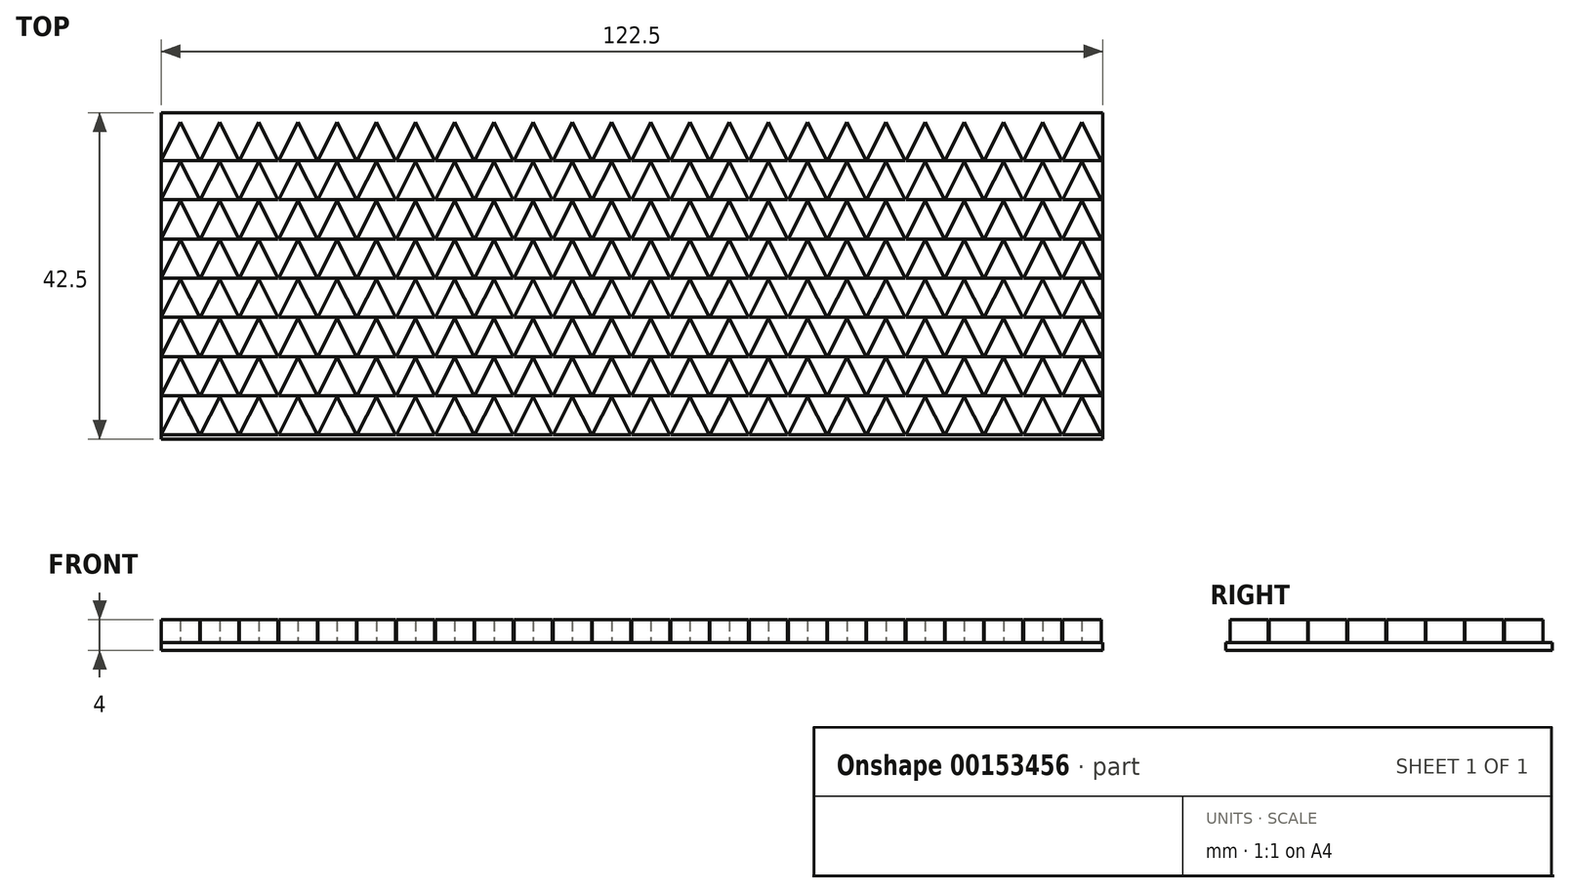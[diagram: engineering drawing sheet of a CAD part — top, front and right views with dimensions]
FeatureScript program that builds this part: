
annotation { "Feature Type Name" : "Feature", "Feature Type Description" : "" }
export const myFeature = defineFeature(function(context is Context, id is Id, definition is map)
    precondition{}
    {
        {
            var Q0;
            Q0=qCreatedBy(makeId("Top.planeOp"),FACE);
            var sketch = newSketch(context, id + "F0", { "sketchPlane" : qUnion([Q0])});
            skLineSegment(sketch, "E0.bottom", {"start": v(61.25, -21.25) * mm, "end": v(-61.25, -21.25) * mm});
            skLineSegment(sketch, "E0.top", {"start": v(61.25, 21.25) * mm, "end": v(-61.25, 21.25) * mm});
            skLineSegment(sketch, "E0.left", {"start": v(61.25, -21.25) * mm, "end": v(61.25, 21.25) * mm});
            skLineSegment(sketch, "E0.right", {"start": v(-61.25, -21.25) * mm, "end": v(-61.25, 21.25) * mm});
            skPoint(sketch, "E0.middle", {"position": v(0, 0) * mm});
            skSolve(sketch);
        }
        {
            var Q0;
            Q0=makeQuery(id+"F0.imprint","IMPRINT",FACE,{"disambiguationData":[TD([[makeQuery(id+"F0.imprint","IMPRINT",EDGE,{"derivedFrom":sQuery(id+"F0.wireOp",EDGE,"E0.bottom")}),-1.0]])]});
            extrude(context, id + "F1", {"entities" : qUnion([Q0]), "depth" : 1 * mm});
        }
        {
            var Q0;
            Q0=makeQuery(id+"F1.opExtrude","CAP_FACE",FACE,{"disambiguationData":[OSD([sQuery(id+"F0.wireOp",EDGE,"E0.bottom"),sQuery(id+"F0.wireOp",EDGE,"E0.top"),sQuery(id+"F0.wireOp",EDGE,"E0.left"),sQuery(id+"F0.wireOp",EDGE,"E0.right")])],"isStart":false});
            var sketch = newSketch(context, id + "F2", { "sketchPlane" : qUnion([Q0])});
            skLineSegment(sketch, "E1.top", {"start": v(-61.25, 15) * mm, "end": v(-56.25, 15) * mm});
            skLineSegment(sketch, "E2", {"start": v(-61.25, 15) * mm, "end": v(-58.75, 20) * mm});
            skLineSegment(sketch, "E3", {"start": v(-58.75, 20) * mm, "end": v(-56.25, 15) * mm});
            skLineSegment(sketch, "E4.0.1.0", {"start": v(-58.75, 14.9) * mm, "end": v(-56.25, 9.9) * mm});
            skLineSegment(sketch, "E4.0.1.1", {"start": v(-61.25, 9.9) * mm, "end": v(-56.25, 9.9) * mm});
            skLineSegment(sketch, "E4.0.1.2", {"start": v(-61.25, 9.9) * mm, "end": v(-58.75, 14.9) * mm});
            skLineSegment(sketch, "E4.0.2.0", {"start": v(-58.75, 9.8) * mm, "end": v(-56.25, 4.8) * mm});
            skLineSegment(sketch, "E4.0.2.1", {"start": v(-61.25, 4.8) * mm, "end": v(-56.25, 4.8) * mm});
            skLineSegment(sketch, "E4.0.2.2", {"start": v(-61.25, 4.8) * mm, "end": v(-58.75, 9.8) * mm});
            skLineSegment(sketch, "E4.0.3.0", {"start": v(-58.75, 4.7) * mm, "end": v(-56.25, -0.3) * mm});
            skLineSegment(sketch, "E4.0.3.1", {"start": v(-61.25, -0.3) * mm, "end": v(-56.25, -0.3) * mm});
            skLineSegment(sketch, "E4.0.3.2", {"start": v(-61.25, -0.3) * mm, "end": v(-58.75, 4.7) * mm});
            skLineSegment(sketch, "E4.0.4.0", {"start": v(-58.75, -0.4) * mm, "end": v(-56.25, -5.4) * mm});
            skLineSegment(sketch, "E4.0.4.1", {"start": v(-61.25, -5.4) * mm, "end": v(-56.25, -5.4) * mm});
            skLineSegment(sketch, "E4.0.4.2", {"start": v(-61.25, -5.4) * mm, "end": v(-58.75, -0.4) * mm});
            skLineSegment(sketch, "E4.0.5.0", {"start": v(-58.75, -5.5) * mm, "end": v(-56.25, -10.5) * mm});
            skLineSegment(sketch, "E4.0.5.1", {"start": v(-61.25, -10.5) * mm, "end": v(-56.25, -10.5) * mm});
            skLineSegment(sketch, "E4.0.5.2", {"start": v(-61.25, -10.5) * mm, "end": v(-58.75, -5.5) * mm});
            skLineSegment(sketch, "E4.0.6.0", {"start": v(-58.75, -10.6) * mm, "end": v(-56.25, -15.6) * mm});
            skLineSegment(sketch, "E4.0.6.1", {"start": v(-61.25, -15.6) * mm, "end": v(-56.25, -15.6) * mm});
            skLineSegment(sketch, "E4.0.6.2", {"start": v(-61.25, -15.6) * mm, "end": v(-58.75, -10.6) * mm});
            skLineSegment(sketch, "E4.0.7.0", {"start": v(-58.75, -15.7) * mm, "end": v(-56.25, -20.7) * mm});
            skLineSegment(sketch, "E4.0.7.1", {"start": v(-61.25, -20.7) * mm, "end": v(-56.25, -20.7) * mm});
            skLineSegment(sketch, "E4.0.7.2", {"start": v(-61.25, -20.7) * mm, "end": v(-58.75, -15.7) * mm});
            skLineSegment(sketch, "E4.1.0.0", {"start": v(-53.65, 20) * mm, "end": v(-51.15, 15) * mm});
            skLineSegment(sketch, "E4.1.0.1", {"start": v(-56.15, 15) * mm, "end": v(-51.15, 15) * mm});
            skLineSegment(sketch, "E4.1.0.2", {"start": v(-56.15, 15) * mm, "end": v(-53.65, 20) * mm});
            skLineSegment(sketch, "E4.1.1.0", {"start": v(-53.65, 14.9) * mm, "end": v(-51.15, 9.9) * mm});
            skLineSegment(sketch, "E4.1.1.1", {"start": v(-56.15, 9.9) * mm, "end": v(-51.15, 9.9) * mm});
            skLineSegment(sketch, "E4.1.1.2", {"start": v(-56.15, 9.9) * mm, "end": v(-53.65, 14.9) * mm});
            skLineSegment(sketch, "E4.1.2.0", {"start": v(-53.65, 9.8) * mm, "end": v(-51.15, 4.8) * mm});
            skLineSegment(sketch, "E4.1.2.1", {"start": v(-56.15, 4.8) * mm, "end": v(-51.15, 4.8) * mm});
            skLineSegment(sketch, "E4.1.2.2", {"start": v(-56.15, 4.8) * mm, "end": v(-53.65, 9.8) * mm});
            skLineSegment(sketch, "E4.1.3.0", {"start": v(-53.65, 4.7) * mm, "end": v(-51.15, -0.3) * mm});
            skLineSegment(sketch, "E4.1.3.1", {"start": v(-56.15, -0.3) * mm, "end": v(-51.15, -0.3) * mm});
            skLineSegment(sketch, "E4.1.3.2", {"start": v(-56.15, -0.3) * mm, "end": v(-53.65, 4.7) * mm});
            skLineSegment(sketch, "E4.1.4.0", {"start": v(-53.65, -0.4) * mm, "end": v(-51.15, -5.4) * mm});
            skLineSegment(sketch, "E4.1.4.1", {"start": v(-56.15, -5.4) * mm, "end": v(-51.15, -5.4) * mm});
            skLineSegment(sketch, "E4.1.4.2", {"start": v(-56.15, -5.4) * mm, "end": v(-53.65, -0.4) * mm});
            skLineSegment(sketch, "E4.1.5.0", {"start": v(-53.65, -5.5) * mm, "end": v(-51.15, -10.5) * mm});
            skLineSegment(sketch, "E4.1.5.1", {"start": v(-56.15, -10.5) * mm, "end": v(-51.15, -10.5) * mm});
            skLineSegment(sketch, "E4.1.5.2", {"start": v(-56.15, -10.5) * mm, "end": v(-53.65, -5.5) * mm});
            skLineSegment(sketch, "E4.1.6.0", {"start": v(-53.65, -10.6) * mm, "end": v(-51.15, -15.6) * mm});
            skLineSegment(sketch, "E4.1.6.1", {"start": v(-56.15, -15.6) * mm, "end": v(-51.15, -15.6) * mm});
            skLineSegment(sketch, "E4.1.6.2", {"start": v(-56.15, -15.6) * mm, "end": v(-53.65, -10.6) * mm});
            skLineSegment(sketch, "E4.1.7.0", {"start": v(-53.65, -15.7) * mm, "end": v(-51.15, -20.7) * mm});
            skLineSegment(sketch, "E4.1.7.1", {"start": v(-56.15, -20.7) * mm, "end": v(-51.15, -20.7) * mm});
            skLineSegment(sketch, "E4.1.7.2", {"start": v(-56.15, -20.7) * mm, "end": v(-53.65, -15.7) * mm});
            skLineSegment(sketch, "E4.2.0.0", {"start": v(-48.55, 20) * mm, "end": v(-46.05, 15) * mm});
            skLineSegment(sketch, "E4.2.0.1", {"start": v(-51.05, 15) * mm, "end": v(-46.05, 15) * mm});
            skLineSegment(sketch, "E4.2.0.2", {"start": v(-51.05, 15) * mm, "end": v(-48.55, 20) * mm});
            skLineSegment(sketch, "E4.2.1.0", {"start": v(-48.55, 14.9) * mm, "end": v(-46.05, 9.9) * mm});
            skLineSegment(sketch, "E4.2.1.1", {"start": v(-51.05, 9.9) * mm, "end": v(-46.05, 9.9) * mm});
            skLineSegment(sketch, "E4.2.1.2", {"start": v(-51.05, 9.9) * mm, "end": v(-48.55, 14.9) * mm});
            skLineSegment(sketch, "E4.2.2.0", {"start": v(-48.55, 9.8) * mm, "end": v(-46.05, 4.8) * mm});
            skLineSegment(sketch, "E4.2.2.1", {"start": v(-51.05, 4.8) * mm, "end": v(-46.05, 4.8) * mm});
            skLineSegment(sketch, "E4.2.2.2", {"start": v(-51.05, 4.8) * mm, "end": v(-48.55, 9.8) * mm});
            skLineSegment(sketch, "E4.2.3.0", {"start": v(-48.55, 4.7) * mm, "end": v(-46.05, -0.3) * mm});
            skLineSegment(sketch, "E4.2.3.1", {"start": v(-51.05, -0.3) * mm, "end": v(-46.05, -0.3) * mm});
            skLineSegment(sketch, "E4.2.3.2", {"start": v(-51.05, -0.3) * mm, "end": v(-48.55, 4.7) * mm});
            skLineSegment(sketch, "E4.2.4.0", {"start": v(-48.55, -0.4) * mm, "end": v(-46.05, -5.4) * mm});
            skLineSegment(sketch, "E4.2.4.1", {"start": v(-51.05, -5.4) * mm, "end": v(-46.05, -5.4) * mm});
            skLineSegment(sketch, "E4.2.4.2", {"start": v(-51.05, -5.4) * mm, "end": v(-48.55, -0.4) * mm});
            skLineSegment(sketch, "E4.2.5.0", {"start": v(-48.55, -5.5) * mm, "end": v(-46.05, -10.5) * mm});
            skLineSegment(sketch, "E4.2.5.1", {"start": v(-51.05, -10.5) * mm, "end": v(-46.05, -10.5) * mm});
            skLineSegment(sketch, "E4.2.5.2", {"start": v(-51.05, -10.5) * mm, "end": v(-48.55, -5.5) * mm});
            skLineSegment(sketch, "E4.2.6.0", {"start": v(-48.55, -10.6) * mm, "end": v(-46.05, -15.6) * mm});
            skLineSegment(sketch, "E4.2.6.1", {"start": v(-51.05, -15.6) * mm, "end": v(-46.05, -15.6) * mm});
            skLineSegment(sketch, "E4.2.6.2", {"start": v(-51.05, -15.6) * mm, "end": v(-48.55, -10.6) * mm});
            skLineSegment(sketch, "E4.2.7.0", {"start": v(-48.55, -15.7) * mm, "end": v(-46.05, -20.7) * mm});
            skLineSegment(sketch, "E4.2.7.1", {"start": v(-51.05, -20.7) * mm, "end": v(-46.05, -20.7) * mm});
            skLineSegment(sketch, "E4.2.7.2", {"start": v(-51.05, -20.7) * mm, "end": v(-48.55, -15.7) * mm});
            skLineSegment(sketch, "E4.3.0.0", {"start": v(-43.45, 20) * mm, "end": v(-40.95, 15) * mm});
            skLineSegment(sketch, "E4.3.0.1", {"start": v(-45.95, 15) * mm, "end": v(-40.95, 15) * mm});
            skLineSegment(sketch, "E4.3.0.2", {"start": v(-45.95, 15) * mm, "end": v(-43.45, 20) * mm});
            skLineSegment(sketch, "E4.3.1.0", {"start": v(-43.45, 14.9) * mm, "end": v(-40.95, 9.9) * mm});
            skLineSegment(sketch, "E4.3.1.1", {"start": v(-45.95, 9.9) * mm, "end": v(-40.95, 9.9) * mm});
            skLineSegment(sketch, "E4.3.1.2", {"start": v(-45.95, 9.9) * mm, "end": v(-43.45, 14.9) * mm});
            skLineSegment(sketch, "E4.3.2.0", {"start": v(-43.45, 9.8) * mm, "end": v(-40.95, 4.8) * mm});
            skLineSegment(sketch, "E4.3.2.1", {"start": v(-45.95, 4.8) * mm, "end": v(-40.95, 4.8) * mm});
            skLineSegment(sketch, "E4.3.2.2", {"start": v(-45.95, 4.8) * mm, "end": v(-43.45, 9.8) * mm});
            skLineSegment(sketch, "E4.3.3.0", {"start": v(-43.45, 4.7) * mm, "end": v(-40.95, -0.3) * mm});
            skLineSegment(sketch, "E4.3.3.1", {"start": v(-45.95, -0.3) * mm, "end": v(-40.95, -0.3) * mm});
            skLineSegment(sketch, "E4.3.3.2", {"start": v(-45.95, -0.3) * mm, "end": v(-43.45, 4.7) * mm});
            skLineSegment(sketch, "E4.3.4.0", {"start": v(-43.45, -0.4) * mm, "end": v(-40.95, -5.4) * mm});
            skLineSegment(sketch, "E4.3.4.1", {"start": v(-45.95, -5.4) * mm, "end": v(-40.95, -5.4) * mm});
            skLineSegment(sketch, "E4.3.4.2", {"start": v(-45.95, -5.4) * mm, "end": v(-43.45, -0.4) * mm});
            skLineSegment(sketch, "E4.3.5.0", {"start": v(-43.45, -5.5) * mm, "end": v(-40.95, -10.5) * mm});
            skLineSegment(sketch, "E4.3.5.1", {"start": v(-45.95, -10.5) * mm, "end": v(-40.95, -10.5) * mm});
            skLineSegment(sketch, "E4.3.5.2", {"start": v(-45.95, -10.5) * mm, "end": v(-43.45, -5.5) * mm});
            skLineSegment(sketch, "E4.3.6.0", {"start": v(-43.45, -10.6) * mm, "end": v(-40.95, -15.6) * mm});
            skLineSegment(sketch, "E4.3.6.1", {"start": v(-45.95, -15.6) * mm, "end": v(-40.95, -15.6) * mm});
            skLineSegment(sketch, "E4.3.6.2", {"start": v(-45.95, -15.6) * mm, "end": v(-43.45, -10.6) * mm});
            skLineSegment(sketch, "E4.3.7.0", {"start": v(-43.45, -15.7) * mm, "end": v(-40.95, -20.7) * mm});
            skLineSegment(sketch, "E4.3.7.1", {"start": v(-45.95, -20.7) * mm, "end": v(-40.95, -20.7) * mm});
            skLineSegment(sketch, "E4.3.7.2", {"start": v(-45.95, -20.7) * mm, "end": v(-43.45, -15.7) * mm});
            skLineSegment(sketch, "E4.4.0.0", {"start": v(-38.35, 20) * mm, "end": v(-35.85, 15) * mm});
            skLineSegment(sketch, "E4.4.0.1", {"start": v(-40.85, 15) * mm, "end": v(-35.85, 15) * mm});
            skLineSegment(sketch, "E4.4.0.2", {"start": v(-40.85, 15) * mm, "end": v(-38.35, 20) * mm});
            skLineSegment(sketch, "E4.4.1.0", {"start": v(-38.35, 14.9) * mm, "end": v(-35.85, 9.9) * mm});
            skLineSegment(sketch, "E4.4.1.1", {"start": v(-40.85, 9.9) * mm, "end": v(-35.85, 9.9) * mm});
            skLineSegment(sketch, "E4.4.1.2", {"start": v(-40.85, 9.9) * mm, "end": v(-38.35, 14.9) * mm});
            skLineSegment(sketch, "E4.4.2.0", {"start": v(-38.35, 9.8) * mm, "end": v(-35.85, 4.8) * mm});
            skLineSegment(sketch, "E4.4.2.1", {"start": v(-40.85, 4.8) * mm, "end": v(-35.85, 4.8) * mm});
            skLineSegment(sketch, "E4.4.2.2", {"start": v(-40.85, 4.8) * mm, "end": v(-38.35, 9.8) * mm});
            skLineSegment(sketch, "E4.4.3.0", {"start": v(-38.35, 4.7) * mm, "end": v(-35.85, -0.3) * mm});
            skLineSegment(sketch, "E4.4.3.1", {"start": v(-40.85, -0.3) * mm, "end": v(-35.85, -0.3) * mm});
            skLineSegment(sketch, "E4.4.3.2", {"start": v(-40.85, -0.3) * mm, "end": v(-38.35, 4.7) * mm});
            skLineSegment(sketch, "E4.4.4.0", {"start": v(-38.35, -0.4) * mm, "end": v(-35.85, -5.4) * mm});
            skLineSegment(sketch, "E4.4.4.1", {"start": v(-40.85, -5.4) * mm, "end": v(-35.85, -5.4) * mm});
            skLineSegment(sketch, "E4.4.4.2", {"start": v(-40.85, -5.4) * mm, "end": v(-38.35, -0.4) * mm});
            skLineSegment(sketch, "E4.4.5.0", {"start": v(-38.35, -5.5) * mm, "end": v(-35.85, -10.5) * mm});
            skLineSegment(sketch, "E4.4.5.1", {"start": v(-40.85, -10.5) * mm, "end": v(-35.85, -10.5) * mm});
            skLineSegment(sketch, "E4.4.5.2", {"start": v(-40.85, -10.5) * mm, "end": v(-38.35, -5.5) * mm});
            skLineSegment(sketch, "E4.4.6.0", {"start": v(-38.35, -10.6) * mm, "end": v(-35.85, -15.6) * mm});
            skLineSegment(sketch, "E4.4.6.1", {"start": v(-40.85, -15.6) * mm, "end": v(-35.85, -15.6) * mm});
            skLineSegment(sketch, "E4.4.6.2", {"start": v(-40.85, -15.6) * mm, "end": v(-38.35, -10.6) * mm});
            skLineSegment(sketch, "E4.4.7.0", {"start": v(-38.35, -15.7) * mm, "end": v(-35.85, -20.7) * mm});
            skLineSegment(sketch, "E4.4.7.1", {"start": v(-40.85, -20.7) * mm, "end": v(-35.85, -20.7) * mm});
            skLineSegment(sketch, "E4.4.7.2", {"start": v(-40.85, -20.7) * mm, "end": v(-38.35, -15.7) * mm});
            skLineSegment(sketch, "E4.5.0.0", {"start": v(-33.25, 20) * mm, "end": v(-30.75, 15) * mm});
            skLineSegment(sketch, "E4.5.0.1", {"start": v(-35.75, 15) * mm, "end": v(-30.75, 15) * mm});
            skLineSegment(sketch, "E4.5.0.2", {"start": v(-35.75, 15) * mm, "end": v(-33.25, 20) * mm});
            skLineSegment(sketch, "E4.5.1.0", {"start": v(-33.25, 14.9) * mm, "end": v(-30.75, 9.9) * mm});
            skLineSegment(sketch, "E4.5.1.1", {"start": v(-35.75, 9.9) * mm, "end": v(-30.75, 9.9) * mm});
            skLineSegment(sketch, "E4.5.1.2", {"start": v(-35.75, 9.9) * mm, "end": v(-33.25, 14.9) * mm});
            skLineSegment(sketch, "E4.5.2.0", {"start": v(-33.25, 9.8) * mm, "end": v(-30.75, 4.8) * mm});
            skLineSegment(sketch, "E4.5.2.1", {"start": v(-35.75, 4.8) * mm, "end": v(-30.75, 4.8) * mm});
            skLineSegment(sketch, "E4.5.2.2", {"start": v(-35.75, 4.8) * mm, "end": v(-33.25, 9.8) * mm});
            skLineSegment(sketch, "E4.5.3.0", {"start": v(-33.25, 4.7) * mm, "end": v(-30.75, -0.3) * mm});
            skLineSegment(sketch, "E4.5.3.1", {"start": v(-35.75, -0.3) * mm, "end": v(-30.75, -0.3) * mm});
            skLineSegment(sketch, "E4.5.3.2", {"start": v(-35.75, -0.3) * mm, "end": v(-33.25, 4.7) * mm});
            skLineSegment(sketch, "E4.5.4.0", {"start": v(-33.25, -0.4) * mm, "end": v(-30.75, -5.4) * mm});
            skLineSegment(sketch, "E4.5.4.1", {"start": v(-35.75, -5.4) * mm, "end": v(-30.75, -5.4) * mm});
            skLineSegment(sketch, "E4.5.4.2", {"start": v(-35.75, -5.4) * mm, "end": v(-33.25, -0.4) * mm});
            skLineSegment(sketch, "E4.5.5.0", {"start": v(-33.25, -5.5) * mm, "end": v(-30.75, -10.5) * mm});
            skLineSegment(sketch, "E4.5.5.1", {"start": v(-35.75, -10.5) * mm, "end": v(-30.75, -10.5) * mm});
            skLineSegment(sketch, "E4.5.5.2", {"start": v(-35.75, -10.5) * mm, "end": v(-33.25, -5.5) * mm});
            skLineSegment(sketch, "E4.5.6.0", {"start": v(-33.25, -10.6) * mm, "end": v(-30.75, -15.6) * mm});
            skLineSegment(sketch, "E4.5.6.1", {"start": v(-35.75, -15.6) * mm, "end": v(-30.75, -15.6) * mm});
            skLineSegment(sketch, "E4.5.6.2", {"start": v(-35.75, -15.6) * mm, "end": v(-33.25, -10.6) * mm});
            skLineSegment(sketch, "E4.5.7.0", {"start": v(-33.25, -15.7) * mm, "end": v(-30.75, -20.7) * mm});
            skLineSegment(sketch, "E4.5.7.1", {"start": v(-35.75, -20.7) * mm, "end": v(-30.75, -20.7) * mm});
            skLineSegment(sketch, "E4.5.7.2", {"start": v(-35.75, -20.7) * mm, "end": v(-33.25, -15.7) * mm});
            skLineSegment(sketch, "E4.6.0.0", {"start": v(-28.15, 20) * mm, "end": v(-25.65, 15) * mm});
            skLineSegment(sketch, "E4.6.0.1", {"start": v(-30.65, 15) * mm, "end": v(-25.65, 15) * mm});
            skLineSegment(sketch, "E4.6.0.2", {"start": v(-30.65, 15) * mm, "end": v(-28.15, 20) * mm});
            skLineSegment(sketch, "E4.6.1.0", {"start": v(-28.15, 14.9) * mm, "end": v(-25.65, 9.9) * mm});
            skLineSegment(sketch, "E4.6.1.1", {"start": v(-30.65, 9.9) * mm, "end": v(-25.65, 9.9) * mm});
            skLineSegment(sketch, "E4.6.1.2", {"start": v(-30.65, 9.9) * mm, "end": v(-28.15, 14.9) * mm});
            skLineSegment(sketch, "E4.6.2.0", {"start": v(-28.15, 9.8) * mm, "end": v(-25.65, 4.8) * mm});
            skLineSegment(sketch, "E4.6.2.1", {"start": v(-30.65, 4.8) * mm, "end": v(-25.65, 4.8) * mm});
            skLineSegment(sketch, "E4.6.2.2", {"start": v(-30.65, 4.8) * mm, "end": v(-28.15, 9.8) * mm});
            skLineSegment(sketch, "E4.6.3.0", {"start": v(-28.15, 4.7) * mm, "end": v(-25.65, -0.3) * mm});
            skLineSegment(sketch, "E4.6.3.1", {"start": v(-30.65, -0.3) * mm, "end": v(-25.65, -0.3) * mm});
            skLineSegment(sketch, "E4.6.3.2", {"start": v(-30.65, -0.3) * mm, "end": v(-28.15, 4.7) * mm});
            skLineSegment(sketch, "E4.6.4.0", {"start": v(-28.15, -0.4) * mm, "end": v(-25.65, -5.4) * mm});
            skLineSegment(sketch, "E4.6.4.1", {"start": v(-30.65, -5.4) * mm, "end": v(-25.65, -5.4) * mm});
            skLineSegment(sketch, "E4.6.4.2", {"start": v(-30.65, -5.4) * mm, "end": v(-28.15, -0.4) * mm});
            skLineSegment(sketch, "E4.6.5.0", {"start": v(-28.15, -5.5) * mm, "end": v(-25.65, -10.5) * mm});
            skLineSegment(sketch, "E4.6.5.1", {"start": v(-30.65, -10.5) * mm, "end": v(-25.65, -10.5) * mm});
            skLineSegment(sketch, "E4.6.5.2", {"start": v(-30.65, -10.5) * mm, "end": v(-28.15, -5.5) * mm});
            skLineSegment(sketch, "E4.6.6.0", {"start": v(-28.15, -10.6) * mm, "end": v(-25.65, -15.6) * mm});
            skLineSegment(sketch, "E4.6.6.1", {"start": v(-30.65, -15.6) * mm, "end": v(-25.65, -15.6) * mm});
            skLineSegment(sketch, "E4.6.6.2", {"start": v(-30.65, -15.6) * mm, "end": v(-28.15, -10.6) * mm});
            skLineSegment(sketch, "E4.6.7.0", {"start": v(-28.15, -15.7) * mm, "end": v(-25.65, -20.7) * mm});
            skLineSegment(sketch, "E4.6.7.1", {"start": v(-30.65, -20.7) * mm, "end": v(-25.65, -20.7) * mm});
            skLineSegment(sketch, "E4.6.7.2", {"start": v(-30.65, -20.7) * mm, "end": v(-28.15, -15.7) * mm});
            skLineSegment(sketch, "E4.7.0.0", {"start": v(-23.05, 20) * mm, "end": v(-20.55, 15) * mm});
            skLineSegment(sketch, "E4.7.0.1", {"start": v(-25.55, 15) * mm, "end": v(-20.55, 15) * mm});
            skLineSegment(sketch, "E4.7.0.2", {"start": v(-25.55, 15) * mm, "end": v(-23.05, 20) * mm});
            skLineSegment(sketch, "E4.7.1.0", {"start": v(-23.05, 14.9) * mm, "end": v(-20.55, 9.9) * mm});
            skLineSegment(sketch, "E4.7.1.1", {"start": v(-25.55, 9.9) * mm, "end": v(-20.55, 9.9) * mm});
            skLineSegment(sketch, "E4.7.1.2", {"start": v(-25.55, 9.9) * mm, "end": v(-23.05, 14.9) * mm});
            skLineSegment(sketch, "E4.7.2.0", {"start": v(-23.05, 9.8) * mm, "end": v(-20.55, 4.8) * mm});
            skLineSegment(sketch, "E4.7.2.1", {"start": v(-25.55, 4.8) * mm, "end": v(-20.55, 4.8) * mm});
            skLineSegment(sketch, "E4.7.2.2", {"start": v(-25.55, 4.8) * mm, "end": v(-23.05, 9.8) * mm});
            skLineSegment(sketch, "E4.7.3.0", {"start": v(-23.05, 4.7) * mm, "end": v(-20.55, -0.3) * mm});
            skLineSegment(sketch, "E4.7.3.1", {"start": v(-25.55, -0.3) * mm, "end": v(-20.55, -0.3) * mm});
            skLineSegment(sketch, "E4.7.3.2", {"start": v(-25.55, -0.3) * mm, "end": v(-23.05, 4.7) * mm});
            skLineSegment(sketch, "E4.7.4.0", {"start": v(-23.05, -0.4) * mm, "end": v(-20.55, -5.4) * mm});
            skLineSegment(sketch, "E4.7.4.1", {"start": v(-25.55, -5.4) * mm, "end": v(-20.55, -5.4) * mm});
            skLineSegment(sketch, "E4.7.4.2", {"start": v(-25.55, -5.4) * mm, "end": v(-23.05, -0.4) * mm});
            skLineSegment(sketch, "E4.7.5.0", {"start": v(-23.05, -5.5) * mm, "end": v(-20.55, -10.5) * mm});
            skLineSegment(sketch, "E4.7.5.1", {"start": v(-25.55, -10.5) * mm, "end": v(-20.55, -10.5) * mm});
            skLineSegment(sketch, "E4.7.5.2", {"start": v(-25.55, -10.5) * mm, "end": v(-23.05, -5.5) * mm});
            skLineSegment(sketch, "E4.7.6.0", {"start": v(-23.05, -10.6) * mm, "end": v(-20.55, -15.6) * mm});
            skLineSegment(sketch, "E4.7.6.1", {"start": v(-25.55, -15.6) * mm, "end": v(-20.55, -15.6) * mm});
            skLineSegment(sketch, "E4.7.6.2", {"start": v(-25.55, -15.6) * mm, "end": v(-23.05, -10.6) * mm});
            skLineSegment(sketch, "E4.7.7.0", {"start": v(-23.05, -15.7) * mm, "end": v(-20.55, -20.7) * mm});
            skLineSegment(sketch, "E4.7.7.1", {"start": v(-25.55, -20.7) * mm, "end": v(-20.55, -20.7) * mm});
            skLineSegment(sketch, "E4.7.7.2", {"start": v(-25.55, -20.7) * mm, "end": v(-23.05, -15.7) * mm});
            skLineSegment(sketch, "E4.8.0.0", {"start": v(-17.95, 20) * mm, "end": v(-15.45, 15) * mm});
            skLineSegment(sketch, "E4.8.0.1", {"start": v(-20.45, 15) * mm, "end": v(-15.45, 15) * mm});
            skLineSegment(sketch, "E4.8.0.2", {"start": v(-20.45, 15) * mm, "end": v(-17.95, 20) * mm});
            skLineSegment(sketch, "E4.8.1.0", {"start": v(-17.95, 14.9) * mm, "end": v(-15.45, 9.9) * mm});
            skLineSegment(sketch, "E4.8.1.1", {"start": v(-20.45, 9.9) * mm, "end": v(-15.45, 9.9) * mm});
            skLineSegment(sketch, "E4.8.1.2", {"start": v(-20.45, 9.9) * mm, "end": v(-17.95, 14.9) * mm});
            skLineSegment(sketch, "E4.8.2.0", {"start": v(-17.95, 9.8) * mm, "end": v(-15.45, 4.8) * mm});
            skLineSegment(sketch, "E4.8.2.1", {"start": v(-20.45, 4.8) * mm, "end": v(-15.45, 4.8) * mm});
            skLineSegment(sketch, "E4.8.2.2", {"start": v(-20.45, 4.8) * mm, "end": v(-17.95, 9.8) * mm});
            skLineSegment(sketch, "E4.8.3.0", {"start": v(-17.95, 4.7) * mm, "end": v(-15.45, -0.3) * mm});
            skLineSegment(sketch, "E4.8.3.1", {"start": v(-20.45, -0.3) * mm, "end": v(-15.45, -0.3) * mm});
            skLineSegment(sketch, "E4.8.3.2", {"start": v(-20.45, -0.3) * mm, "end": v(-17.95, 4.7) * mm});
            skLineSegment(sketch, "E4.8.4.0", {"start": v(-17.95, -0.4) * mm, "end": v(-15.45, -5.4) * mm});
            skLineSegment(sketch, "E4.8.4.1", {"start": v(-20.45, -5.4) * mm, "end": v(-15.45, -5.4) * mm});
            skLineSegment(sketch, "E4.8.4.2", {"start": v(-20.45, -5.4) * mm, "end": v(-17.95, -0.4) * mm});
            skLineSegment(sketch, "E4.8.5.0", {"start": v(-17.95, -5.5) * mm, "end": v(-15.45, -10.5) * mm});
            skLineSegment(sketch, "E4.8.5.1", {"start": v(-20.45, -10.5) * mm, "end": v(-15.45, -10.5) * mm});
            skLineSegment(sketch, "E4.8.5.2", {"start": v(-20.45, -10.5) * mm, "end": v(-17.95, -5.5) * mm});
            skLineSegment(sketch, "E4.8.6.0", {"start": v(-17.95, -10.6) * mm, "end": v(-15.45, -15.6) * mm});
            skLineSegment(sketch, "E4.8.6.1", {"start": v(-20.45, -15.6) * mm, "end": v(-15.45, -15.6) * mm});
            skLineSegment(sketch, "E4.8.6.2", {"start": v(-20.45, -15.6) * mm, "end": v(-17.95, -10.6) * mm});
            skLineSegment(sketch, "E4.8.7.0", {"start": v(-17.95, -15.7) * mm, "end": v(-15.45, -20.7) * mm});
            skLineSegment(sketch, "E4.8.7.1", {"start": v(-20.45, -20.7) * mm, "end": v(-15.45, -20.7) * mm});
            skLineSegment(sketch, "E4.8.7.2", {"start": v(-20.45, -20.7) * mm, "end": v(-17.95, -15.7) * mm});
            skLineSegment(sketch, "E4.9.0.0", {"start": v(-12.85, 20) * mm, "end": v(-10.35, 15) * mm});
            skLineSegment(sketch, "E4.9.0.1", {"start": v(-15.35, 15) * mm, "end": v(-10.35, 15) * mm});
            skLineSegment(sketch, "E4.9.0.2", {"start": v(-15.35, 15) * mm, "end": v(-12.85, 20) * mm});
            skLineSegment(sketch, "E4.9.1.0", {"start": v(-12.85, 14.9) * mm, "end": v(-10.35, 9.9) * mm});
            skLineSegment(sketch, "E4.9.1.1", {"start": v(-15.35, 9.9) * mm, "end": v(-10.35, 9.9) * mm});
            skLineSegment(sketch, "E4.9.1.2", {"start": v(-15.35, 9.9) * mm, "end": v(-12.85, 14.9) * mm});
            skLineSegment(sketch, "E4.9.2.0", {"start": v(-12.85, 9.8) * mm, "end": v(-10.35, 4.8) * mm});
            skLineSegment(sketch, "E4.9.2.1", {"start": v(-15.35, 4.8) * mm, "end": v(-10.35, 4.8) * mm});
            skLineSegment(sketch, "E4.9.2.2", {"start": v(-15.35, 4.8) * mm, "end": v(-12.85, 9.8) * mm});
            skLineSegment(sketch, "E4.9.3.0", {"start": v(-12.85, 4.7) * mm, "end": v(-10.35, -0.3) * mm});
            skLineSegment(sketch, "E4.9.3.1", {"start": v(-15.35, -0.3) * mm, "end": v(-10.35, -0.3) * mm});
            skLineSegment(sketch, "E4.9.3.2", {"start": v(-15.35, -0.3) * mm, "end": v(-12.85, 4.7) * mm});
            skLineSegment(sketch, "E4.9.4.0", {"start": v(-12.85, -0.4) * mm, "end": v(-10.35, -5.4) * mm});
            skLineSegment(sketch, "E4.9.4.1", {"start": v(-15.35, -5.4) * mm, "end": v(-10.35, -5.4) * mm});
            skLineSegment(sketch, "E4.9.4.2", {"start": v(-15.35, -5.4) * mm, "end": v(-12.85, -0.4) * mm});
            skLineSegment(sketch, "E4.9.5.0", {"start": v(-12.85, -5.5) * mm, "end": v(-10.35, -10.5) * mm});
            skLineSegment(sketch, "E4.9.5.1", {"start": v(-15.35, -10.5) * mm, "end": v(-10.35, -10.5) * mm});
            skLineSegment(sketch, "E4.9.5.2", {"start": v(-15.35, -10.5) * mm, "end": v(-12.85, -5.5) * mm});
            skLineSegment(sketch, "E4.9.6.0", {"start": v(-12.85, -10.6) * mm, "end": v(-10.35, -15.6) * mm});
            skLineSegment(sketch, "E4.9.6.1", {"start": v(-15.35, -15.6) * mm, "end": v(-10.35, -15.6) * mm});
            skLineSegment(sketch, "E4.9.6.2", {"start": v(-15.35, -15.6) * mm, "end": v(-12.85, -10.6) * mm});
            skLineSegment(sketch, "E4.9.7.0", {"start": v(-12.85, -15.7) * mm, "end": v(-10.35, -20.7) * mm});
            skLineSegment(sketch, "E4.9.7.1", {"start": v(-15.35, -20.7) * mm, "end": v(-10.35, -20.7) * mm});
            skLineSegment(sketch, "E4.9.7.2", {"start": v(-15.35, -20.7) * mm, "end": v(-12.85, -15.7) * mm});
            skLineSegment(sketch, "E4.10.0.0", {"start": v(-7.75, 20) * mm, "end": v(-5.25, 15) * mm});
            skLineSegment(sketch, "E4.10.0.1", {"start": v(-10.25, 15) * mm, "end": v(-5.25, 15) * mm});
            skLineSegment(sketch, "E4.10.0.2", {"start": v(-10.25, 15) * mm, "end": v(-7.75, 20) * mm});
            skLineSegment(sketch, "E4.10.1.0", {"start": v(-7.75, 14.9) * mm, "end": v(-5.25, 9.9) * mm});
            skLineSegment(sketch, "E4.10.1.1", {"start": v(-10.25, 9.9) * mm, "end": v(-5.25, 9.9) * mm});
            skLineSegment(sketch, "E4.10.1.2", {"start": v(-10.25, 9.9) * mm, "end": v(-7.75, 14.9) * mm});
            skLineSegment(sketch, "E4.10.2.0", {"start": v(-7.75, 9.8) * mm, "end": v(-5.25, 4.8) * mm});
            skLineSegment(sketch, "E4.10.2.1", {"start": v(-10.25, 4.8) * mm, "end": v(-5.25, 4.8) * mm});
            skLineSegment(sketch, "E4.10.2.2", {"start": v(-10.25, 4.8) * mm, "end": v(-7.75, 9.8) * mm});
            skLineSegment(sketch, "E4.10.3.0", {"start": v(-7.75, 4.7) * mm, "end": v(-5.25, -0.3) * mm});
            skLineSegment(sketch, "E4.10.3.1", {"start": v(-10.25, -0.3) * mm, "end": v(-5.25, -0.3) * mm});
            skLineSegment(sketch, "E4.10.3.2", {"start": v(-10.25, -0.3) * mm, "end": v(-7.75, 4.7) * mm});
            skLineSegment(sketch, "E4.10.4.0", {"start": v(-7.75, -0.4) * mm, "end": v(-5.25, -5.4) * mm});
            skLineSegment(sketch, "E4.10.4.1", {"start": v(-10.25, -5.4) * mm, "end": v(-5.25, -5.4) * mm});
            skLineSegment(sketch, "E4.10.4.2", {"start": v(-10.25, -5.4) * mm, "end": v(-7.75, -0.4) * mm});
            skLineSegment(sketch, "E4.10.5.0", {"start": v(-7.75, -5.5) * mm, "end": v(-5.25, -10.5) * mm});
            skLineSegment(sketch, "E4.10.5.1", {"start": v(-10.25, -10.5) * mm, "end": v(-5.25, -10.5) * mm});
            skLineSegment(sketch, "E4.10.5.2", {"start": v(-10.25, -10.5) * mm, "end": v(-7.75, -5.5) * mm});
            skLineSegment(sketch, "E4.10.6.0", {"start": v(-7.75, -10.6) * mm, "end": v(-5.25, -15.6) * mm});
            skLineSegment(sketch, "E4.10.6.1", {"start": v(-10.25, -15.6) * mm, "end": v(-5.25, -15.6) * mm});
            skLineSegment(sketch, "E4.10.6.2", {"start": v(-10.25, -15.6) * mm, "end": v(-7.75, -10.6) * mm});
            skLineSegment(sketch, "E4.10.7.0", {"start": v(-7.75, -15.7) * mm, "end": v(-5.25, -20.7) * mm});
            skLineSegment(sketch, "E4.10.7.1", {"start": v(-10.25, -20.7) * mm, "end": v(-5.25, -20.7) * mm});
            skLineSegment(sketch, "E4.10.7.2", {"start": v(-10.25, -20.7) * mm, "end": v(-7.75, -15.7) * mm});
            skLineSegment(sketch, "E4.11.0.0", {"start": v(-2.65, 20) * mm, "end": v(-0.15, 15) * mm});
            skLineSegment(sketch, "E4.11.0.1", {"start": v(-5.15, 15) * mm, "end": v(-0.15, 15) * mm});
            skLineSegment(sketch, "E4.11.0.2", {"start": v(-5.15, 15) * mm, "end": v(-2.65, 20) * mm});
            skLineSegment(sketch, "E4.11.1.0", {"start": v(-2.65, 14.9) * mm, "end": v(-0.15, 9.9) * mm});
            skLineSegment(sketch, "E4.11.1.1", {"start": v(-5.15, 9.9) * mm, "end": v(-0.15, 9.9) * mm});
            skLineSegment(sketch, "E4.11.1.2", {"start": v(-5.15, 9.9) * mm, "end": v(-2.65, 14.9) * mm});
            skLineSegment(sketch, "E4.11.2.0", {"start": v(-2.65, 9.8) * mm, "end": v(-0.15, 4.8) * mm});
            skLineSegment(sketch, "E4.11.2.1", {"start": v(-5.15, 4.8) * mm, "end": v(-0.15, 4.8) * mm});
            skLineSegment(sketch, "E4.11.2.2", {"start": v(-5.15, 4.8) * mm, "end": v(-2.65, 9.8) * mm});
            skLineSegment(sketch, "E4.11.3.0", {"start": v(-2.65, 4.7) * mm, "end": v(-0.15, -0.3) * mm});
            skLineSegment(sketch, "E4.11.3.1", {"start": v(-5.15, -0.3) * mm, "end": v(-0.15, -0.3) * mm});
            skLineSegment(sketch, "E4.11.3.2", {"start": v(-5.15, -0.3) * mm, "end": v(-2.65, 4.7) * mm});
            skLineSegment(sketch, "E4.11.4.0", {"start": v(-2.65, -0.4) * mm, "end": v(-0.15, -5.4) * mm});
            skLineSegment(sketch, "E4.11.4.1", {"start": v(-5.15, -5.4) * mm, "end": v(-0.15, -5.4) * mm});
            skLineSegment(sketch, "E4.11.4.2", {"start": v(-5.15, -5.4) * mm, "end": v(-2.65, -0.4) * mm});
            skLineSegment(sketch, "E4.11.5.0", {"start": v(-2.65, -5.5) * mm, "end": v(-0.15, -10.5) * mm});
            skLineSegment(sketch, "E4.11.5.1", {"start": v(-5.15, -10.5) * mm, "end": v(-0.15, -10.5) * mm});
            skLineSegment(sketch, "E4.11.5.2", {"start": v(-5.15, -10.5) * mm, "end": v(-2.65, -5.5) * mm});
            skLineSegment(sketch, "E4.11.6.0", {"start": v(-2.65, -10.6) * mm, "end": v(-0.15, -15.6) * mm});
            skLineSegment(sketch, "E4.11.6.1", {"start": v(-5.15, -15.6) * mm, "end": v(-0.15, -15.6) * mm});
            skLineSegment(sketch, "E4.11.6.2", {"start": v(-5.15, -15.6) * mm, "end": v(-2.65, -10.6) * mm});
            skLineSegment(sketch, "E4.11.7.0", {"start": v(-2.65, -15.7) * mm, "end": v(-0.15, -20.7) * mm});
            skLineSegment(sketch, "E4.11.7.1", {"start": v(-5.15, -20.7) * mm, "end": v(-0.15, -20.7) * mm});
            skLineSegment(sketch, "E4.11.7.2", {"start": v(-5.15, -20.7) * mm, "end": v(-2.65, -15.7) * mm});
            skLineSegment(sketch, "E4.12.0.0", {"start": v(2.45, 20) * mm, "end": v(4.95, 15) * mm});
            skLineSegment(sketch, "E4.12.0.1", {"start": v(-0.05, 15) * mm, "end": v(4.95, 15) * mm});
            skLineSegment(sketch, "E4.12.0.2", {"start": v(-0.05, 15) * mm, "end": v(2.45, 20) * mm});
            skLineSegment(sketch, "E4.12.1.0", {"start": v(2.45, 14.9) * mm, "end": v(4.95, 9.9) * mm});
            skLineSegment(sketch, "E4.12.1.1", {"start": v(-0.05, 9.9) * mm, "end": v(4.95, 9.9) * mm});
            skLineSegment(sketch, "E4.12.1.2", {"start": v(-0.05, 9.9) * mm, "end": v(2.45, 14.9) * mm});
            skLineSegment(sketch, "E4.12.2.0", {"start": v(2.45, 9.8) * mm, "end": v(4.95, 4.8) * mm});
            skLineSegment(sketch, "E4.12.2.1", {"start": v(-0.05, 4.8) * mm, "end": v(4.95, 4.8) * mm});
            skLineSegment(sketch, "E4.12.2.2", {"start": v(-0.05, 4.8) * mm, "end": v(2.45, 9.8) * mm});
            skLineSegment(sketch, "E4.12.3.0", {"start": v(2.45, 4.7) * mm, "end": v(4.95, -0.3) * mm});
            skLineSegment(sketch, "E4.12.3.1", {"start": v(-0.05, -0.3) * mm, "end": v(4.95, -0.3) * mm});
            skLineSegment(sketch, "E4.12.3.2", {"start": v(-0.05, -0.3) * mm, "end": v(2.45, 4.7) * mm});
            skLineSegment(sketch, "E4.12.4.0", {"start": v(2.45, -0.4) * mm, "end": v(4.95, -5.4) * mm});
            skLineSegment(sketch, "E4.12.4.1", {"start": v(-0.05, -5.4) * mm, "end": v(4.95, -5.4) * mm});
            skLineSegment(sketch, "E4.12.4.2", {"start": v(-0.05, -5.4) * mm, "end": v(2.45, -0.4) * mm});
            skLineSegment(sketch, "E4.12.5.0", {"start": v(2.45, -5.5) * mm, "end": v(4.95, -10.5) * mm});
            skLineSegment(sketch, "E4.12.5.1", {"start": v(-0.05, -10.5) * mm, "end": v(4.95, -10.5) * mm});
            skLineSegment(sketch, "E4.12.5.2", {"start": v(-0.05, -10.5) * mm, "end": v(2.45, -5.5) * mm});
            skLineSegment(sketch, "E4.12.6.0", {"start": v(2.45, -10.6) * mm, "end": v(4.95, -15.6) * mm});
            skLineSegment(sketch, "E4.12.6.1", {"start": v(-0.05, -15.6) * mm, "end": v(4.95, -15.6) * mm});
            skLineSegment(sketch, "E4.12.6.2", {"start": v(-0.05, -15.6) * mm, "end": v(2.45, -10.6) * mm});
            skLineSegment(sketch, "E4.12.7.0", {"start": v(2.45, -15.7) * mm, "end": v(4.95, -20.7) * mm});
            skLineSegment(sketch, "E4.12.7.1", {"start": v(-0.05, -20.7) * mm, "end": v(4.95, -20.7) * mm});
            skLineSegment(sketch, "E4.12.7.2", {"start": v(-0.05, -20.7) * mm, "end": v(2.45, -15.7) * mm});
            skLineSegment(sketch, "E4.13.0.0", {"start": v(7.55, 20) * mm, "end": v(10.05, 15) * mm});
            skLineSegment(sketch, "E4.13.0.1", {"start": v(5.05, 15) * mm, "end": v(10.05, 15) * mm});
            skLineSegment(sketch, "E4.13.0.2", {"start": v(5.05, 15) * mm, "end": v(7.55, 20) * mm});
            skLineSegment(sketch, "E4.13.1.0", {"start": v(7.55, 14.9) * mm, "end": v(10.05, 9.9) * mm});
            skLineSegment(sketch, "E4.13.1.1", {"start": v(5.05, 9.9) * mm, "end": v(10.05, 9.9) * mm});
            skLineSegment(sketch, "E4.13.1.2", {"start": v(5.05, 9.9) * mm, "end": v(7.55, 14.9) * mm});
            skLineSegment(sketch, "E4.13.2.0", {"start": v(7.55, 9.8) * mm, "end": v(10.05, 4.8) * mm});
            skLineSegment(sketch, "E4.13.2.1", {"start": v(5.05, 4.8) * mm, "end": v(10.05, 4.8) * mm});
            skLineSegment(sketch, "E4.13.2.2", {"start": v(5.05, 4.8) * mm, "end": v(7.55, 9.8) * mm});
            skLineSegment(sketch, "E4.13.3.0", {"start": v(7.55, 4.7) * mm, "end": v(10.05, -0.3) * mm});
            skLineSegment(sketch, "E4.13.3.1", {"start": v(5.05, -0.3) * mm, "end": v(10.05, -0.3) * mm});
            skLineSegment(sketch, "E4.13.3.2", {"start": v(5.05, -0.3) * mm, "end": v(7.55, 4.7) * mm});
            skLineSegment(sketch, "E4.13.4.0", {"start": v(7.55, -0.4) * mm, "end": v(10.05, -5.4) * mm});
            skLineSegment(sketch, "E4.13.4.1", {"start": v(5.05, -5.4) * mm, "end": v(10.05, -5.4) * mm});
            skLineSegment(sketch, "E4.13.4.2", {"start": v(5.05, -5.4) * mm, "end": v(7.55, -0.4) * mm});
            skLineSegment(sketch, "E4.13.5.0", {"start": v(7.55, -5.5) * mm, "end": v(10.05, -10.5) * mm});
            skLineSegment(sketch, "E4.13.5.1", {"start": v(5.05, -10.5) * mm, "end": v(10.05, -10.5) * mm});
            skLineSegment(sketch, "E4.13.5.2", {"start": v(5.05, -10.5) * mm, "end": v(7.55, -5.5) * mm});
            skLineSegment(sketch, "E4.13.6.0", {"start": v(7.55, -10.6) * mm, "end": v(10.05, -15.6) * mm});
            skLineSegment(sketch, "E4.13.6.1", {"start": v(5.05, -15.6) * mm, "end": v(10.05, -15.6) * mm});
            skLineSegment(sketch, "E4.13.6.2", {"start": v(5.05, -15.6) * mm, "end": v(7.55, -10.6) * mm});
            skLineSegment(sketch, "E4.13.7.0", {"start": v(7.55, -15.7) * mm, "end": v(10.05, -20.7) * mm});
            skLineSegment(sketch, "E4.13.7.1", {"start": v(5.05, -20.7) * mm, "end": v(10.05, -20.7) * mm});
            skLineSegment(sketch, "E4.13.7.2", {"start": v(5.05, -20.7) * mm, "end": v(7.55, -15.7) * mm});
            skLineSegment(sketch, "E4.14.0.0", {"start": v(12.65, 20) * mm, "end": v(15.15, 15) * mm});
            skLineSegment(sketch, "E4.14.0.1", {"start": v(10.15, 15) * mm, "end": v(15.15, 15) * mm});
            skLineSegment(sketch, "E4.14.0.2", {"start": v(10.15, 15) * mm, "end": v(12.65, 20) * mm});
            skLineSegment(sketch, "E4.14.1.0", {"start": v(12.65, 14.9) * mm, "end": v(15.15, 9.9) * mm});
            skLineSegment(sketch, "E4.14.1.1", {"start": v(10.15, 9.9) * mm, "end": v(15.15, 9.9) * mm});
            skLineSegment(sketch, "E4.14.1.2", {"start": v(10.15, 9.9) * mm, "end": v(12.65, 14.9) * mm});
            skLineSegment(sketch, "E4.14.2.0", {"start": v(12.65, 9.8) * mm, "end": v(15.15, 4.8) * mm});
            skLineSegment(sketch, "E4.14.2.1", {"start": v(10.15, 4.8) * mm, "end": v(15.15, 4.8) * mm});
            skLineSegment(sketch, "E4.14.2.2", {"start": v(10.15, 4.8) * mm, "end": v(12.65, 9.8) * mm});
            skLineSegment(sketch, "E4.14.3.0", {"start": v(12.65, 4.7) * mm, "end": v(15.15, -0.3) * mm});
            skLineSegment(sketch, "E4.14.3.1", {"start": v(10.15, -0.3) * mm, "end": v(15.15, -0.3) * mm});
            skLineSegment(sketch, "E4.14.3.2", {"start": v(10.15, -0.3) * mm, "end": v(12.65, 4.7) * mm});
            skLineSegment(sketch, "E4.14.4.0", {"start": v(12.65, -0.4) * mm, "end": v(15.15, -5.4) * mm});
            skLineSegment(sketch, "E4.14.4.1", {"start": v(10.15, -5.4) * mm, "end": v(15.15, -5.4) * mm});
            skLineSegment(sketch, "E4.14.4.2", {"start": v(10.15, -5.4) * mm, "end": v(12.65, -0.4) * mm});
            skLineSegment(sketch, "E4.14.5.0", {"start": v(12.65, -5.5) * mm, "end": v(15.15, -10.5) * mm});
            skLineSegment(sketch, "E4.14.5.1", {"start": v(10.15, -10.5) * mm, "end": v(15.15, -10.5) * mm});
            skLineSegment(sketch, "E4.14.5.2", {"start": v(10.15, -10.5) * mm, "end": v(12.65, -5.5) * mm});
            skLineSegment(sketch, "E4.14.6.0", {"start": v(12.65, -10.6) * mm, "end": v(15.15, -15.6) * mm});
            skLineSegment(sketch, "E4.14.6.1", {"start": v(10.15, -15.6) * mm, "end": v(15.15, -15.6) * mm});
            skLineSegment(sketch, "E4.14.6.2", {"start": v(10.15, -15.6) * mm, "end": v(12.65, -10.6) * mm});
            skLineSegment(sketch, "E4.14.7.0", {"start": v(12.65, -15.7) * mm, "end": v(15.15, -20.7) * mm});
            skLineSegment(sketch, "E4.14.7.1", {"start": v(10.15, -20.7) * mm, "end": v(15.15, -20.7) * mm});
            skLineSegment(sketch, "E4.14.7.2", {"start": v(10.15, -20.7) * mm, "end": v(12.65, -15.7) * mm});
            skLineSegment(sketch, "E4.15.0.0", {"start": v(17.75, 20) * mm, "end": v(20.25, 15) * mm});
            skLineSegment(sketch, "E4.15.0.1", {"start": v(15.25, 15) * mm, "end": v(20.25, 15) * mm});
            skLineSegment(sketch, "E4.15.0.2", {"start": v(15.25, 15) * mm, "end": v(17.75, 20) * mm});
            skLineSegment(sketch, "E4.15.1.0", {"start": v(17.75, 14.9) * mm, "end": v(20.25, 9.9) * mm});
            skLineSegment(sketch, "E4.15.1.1", {"start": v(15.25, 9.9) * mm, "end": v(20.25, 9.9) * mm});
            skLineSegment(sketch, "E4.15.1.2", {"start": v(15.25, 9.9) * mm, "end": v(17.75, 14.9) * mm});
            skLineSegment(sketch, "E4.15.2.0", {"start": v(17.75, 9.8) * mm, "end": v(20.25, 4.8) * mm});
            skLineSegment(sketch, "E4.15.2.1", {"start": v(15.25, 4.8) * mm, "end": v(20.25, 4.8) * mm});
            skLineSegment(sketch, "E4.15.2.2", {"start": v(15.25, 4.8) * mm, "end": v(17.75, 9.8) * mm});
            skLineSegment(sketch, "E4.15.3.0", {"start": v(17.75, 4.7) * mm, "end": v(20.25, -0.3) * mm});
            skLineSegment(sketch, "E4.15.3.1", {"start": v(15.25, -0.3) * mm, "end": v(20.25, -0.3) * mm});
            skLineSegment(sketch, "E4.15.3.2", {"start": v(15.25, -0.3) * mm, "end": v(17.75, 4.7) * mm});
            skLineSegment(sketch, "E4.15.4.0", {"start": v(17.75, -0.4) * mm, "end": v(20.25, -5.4) * mm});
            skLineSegment(sketch, "E4.15.4.1", {"start": v(15.25, -5.4) * mm, "end": v(20.25, -5.4) * mm});
            skLineSegment(sketch, "E4.15.4.2", {"start": v(15.25, -5.4) * mm, "end": v(17.75, -0.4) * mm});
            skLineSegment(sketch, "E4.15.5.0", {"start": v(17.75, -5.5) * mm, "end": v(20.25, -10.5) * mm});
            skLineSegment(sketch, "E4.15.5.1", {"start": v(15.25, -10.5) * mm, "end": v(20.25, -10.5) * mm});
            skLineSegment(sketch, "E4.15.5.2", {"start": v(15.25, -10.5) * mm, "end": v(17.75, -5.5) * mm});
            skLineSegment(sketch, "E4.15.6.0", {"start": v(17.75, -10.6) * mm, "end": v(20.25, -15.6) * mm});
            skLineSegment(sketch, "E4.15.6.1", {"start": v(15.25, -15.6) * mm, "end": v(20.25, -15.6) * mm});
            skLineSegment(sketch, "E4.15.6.2", {"start": v(15.25, -15.6) * mm, "end": v(17.75, -10.6) * mm});
            skLineSegment(sketch, "E4.15.7.0", {"start": v(17.75, -15.7) * mm, "end": v(20.25, -20.7) * mm});
            skLineSegment(sketch, "E4.15.7.1", {"start": v(15.25, -20.7) * mm, "end": v(20.25, -20.7) * mm});
            skLineSegment(sketch, "E4.15.7.2", {"start": v(15.25, -20.7) * mm, "end": v(17.75, -15.7) * mm});
            skLineSegment(sketch, "E4.16.0.0", {"start": v(22.85, 20) * mm, "end": v(25.35, 15) * mm});
            skLineSegment(sketch, "E4.16.0.1", {"start": v(20.35, 15) * mm, "end": v(25.35, 15) * mm});
            skLineSegment(sketch, "E4.16.0.2", {"start": v(20.35, 15) * mm, "end": v(22.85, 20) * mm});
            skLineSegment(sketch, "E4.16.1.0", {"start": v(22.85, 14.9) * mm, "end": v(25.35, 9.9) * mm});
            skLineSegment(sketch, "E4.16.1.1", {"start": v(20.35, 9.9) * mm, "end": v(25.35, 9.9) * mm});
            skLineSegment(sketch, "E4.16.1.2", {"start": v(20.35, 9.9) * mm, "end": v(22.85, 14.9) * mm});
            skLineSegment(sketch, "E4.16.2.0", {"start": v(22.85, 9.8) * mm, "end": v(25.35, 4.8) * mm});
            skLineSegment(sketch, "E4.16.2.1", {"start": v(20.35, 4.8) * mm, "end": v(25.35, 4.8) * mm});
            skLineSegment(sketch, "E4.16.2.2", {"start": v(20.35, 4.8) * mm, "end": v(22.85, 9.8) * mm});
            skLineSegment(sketch, "E4.16.3.0", {"start": v(22.85, 4.7) * mm, "end": v(25.35, -0.3) * mm});
            skLineSegment(sketch, "E4.16.3.1", {"start": v(20.35, -0.3) * mm, "end": v(25.35, -0.3) * mm});
            skLineSegment(sketch, "E4.16.3.2", {"start": v(20.35, -0.3) * mm, "end": v(22.85, 4.7) * mm});
            skLineSegment(sketch, "E4.16.4.0", {"start": v(22.85, -0.4) * mm, "end": v(25.35, -5.4) * mm});
            skLineSegment(sketch, "E4.16.4.1", {"start": v(20.35, -5.4) * mm, "end": v(25.35, -5.4) * mm});
            skLineSegment(sketch, "E4.16.4.2", {"start": v(20.35, -5.4) * mm, "end": v(22.85, -0.4) * mm});
            skLineSegment(sketch, "E4.16.5.0", {"start": v(22.85, -5.5) * mm, "end": v(25.35, -10.5) * mm});
            skLineSegment(sketch, "E4.16.5.1", {"start": v(20.35, -10.5) * mm, "end": v(25.35, -10.5) * mm});
            skLineSegment(sketch, "E4.16.5.2", {"start": v(20.35, -10.5) * mm, "end": v(22.85, -5.5) * mm});
            skLineSegment(sketch, "E4.16.6.0", {"start": v(22.85, -10.6) * mm, "end": v(25.35, -15.6) * mm});
            skLineSegment(sketch, "E4.16.6.1", {"start": v(20.35, -15.6) * mm, "end": v(25.35, -15.6) * mm});
            skLineSegment(sketch, "E4.16.6.2", {"start": v(20.35, -15.6) * mm, "end": v(22.85, -10.6) * mm});
            skLineSegment(sketch, "E4.16.7.0", {"start": v(22.85, -15.7) * mm, "end": v(25.35, -20.7) * mm});
            skLineSegment(sketch, "E4.16.7.1", {"start": v(20.35, -20.7) * mm, "end": v(25.35, -20.7) * mm});
            skLineSegment(sketch, "E4.16.7.2", {"start": v(20.35, -20.7) * mm, "end": v(22.85, -15.7) * mm});
            skLineSegment(sketch, "E4.17.0.0", {"start": v(27.95, 20) * mm, "end": v(30.45, 15) * mm});
            skLineSegment(sketch, "E4.17.0.1", {"start": v(25.45, 15) * mm, "end": v(30.45, 15) * mm});
            skLineSegment(sketch, "E4.17.0.2", {"start": v(25.45, 15) * mm, "end": v(27.95, 20) * mm});
            skLineSegment(sketch, "E4.17.1.0", {"start": v(27.95, 14.9) * mm, "end": v(30.45, 9.9) * mm});
            skLineSegment(sketch, "E4.17.1.1", {"start": v(25.45, 9.9) * mm, "end": v(30.45, 9.9) * mm});
            skLineSegment(sketch, "E4.17.1.2", {"start": v(25.45, 9.9) * mm, "end": v(27.95, 14.9) * mm});
            skLineSegment(sketch, "E4.17.2.0", {"start": v(27.95, 9.8) * mm, "end": v(30.45, 4.8) * mm});
            skLineSegment(sketch, "E4.17.2.1", {"start": v(25.45, 4.8) * mm, "end": v(30.45, 4.8) * mm});
            skLineSegment(sketch, "E4.17.2.2", {"start": v(25.45, 4.8) * mm, "end": v(27.95, 9.8) * mm});
            skLineSegment(sketch, "E4.17.3.0", {"start": v(27.95, 4.7) * mm, "end": v(30.45, -0.3) * mm});
            skLineSegment(sketch, "E4.17.3.1", {"start": v(25.45, -0.3) * mm, "end": v(30.45, -0.3) * mm});
            skLineSegment(sketch, "E4.17.3.2", {"start": v(25.45, -0.3) * mm, "end": v(27.95, 4.7) * mm});
            skLineSegment(sketch, "E4.17.4.0", {"start": v(27.95, -0.4) * mm, "end": v(30.45, -5.4) * mm});
            skLineSegment(sketch, "E4.17.4.1", {"start": v(25.45, -5.4) * mm, "end": v(30.45, -5.4) * mm});
            skLineSegment(sketch, "E4.17.4.2", {"start": v(25.45, -5.4) * mm, "end": v(27.95, -0.4) * mm});
            skLineSegment(sketch, "E4.17.5.0", {"start": v(27.95, -5.5) * mm, "end": v(30.45, -10.5) * mm});
            skLineSegment(sketch, "E4.17.5.1", {"start": v(25.45, -10.5) * mm, "end": v(30.45, -10.5) * mm});
            skLineSegment(sketch, "E4.17.5.2", {"start": v(25.45, -10.5) * mm, "end": v(27.95, -5.5) * mm});
            skLineSegment(sketch, "E4.17.6.0", {"start": v(27.95, -10.6) * mm, "end": v(30.45, -15.6) * mm});
            skLineSegment(sketch, "E4.17.6.1", {"start": v(25.45, -15.6) * mm, "end": v(30.45, -15.6) * mm});
            skLineSegment(sketch, "E4.17.6.2", {"start": v(25.45, -15.6) * mm, "end": v(27.95, -10.6) * mm});
            skLineSegment(sketch, "E4.17.7.0", {"start": v(27.95, -15.7) * mm, "end": v(30.45, -20.7) * mm});
            skLineSegment(sketch, "E4.17.7.1", {"start": v(25.45, -20.7) * mm, "end": v(30.45, -20.7) * mm});
            skLineSegment(sketch, "E4.17.7.2", {"start": v(25.45, -20.7) * mm, "end": v(27.95, -15.7) * mm});
            skLineSegment(sketch, "E4.18.0.0", {"start": v(33.05, 20) * mm, "end": v(35.55, 15) * mm});
            skLineSegment(sketch, "E4.18.0.1", {"start": v(30.55, 15) * mm, "end": v(35.55, 15) * mm});
            skLineSegment(sketch, "E4.18.0.2", {"start": v(30.55, 15) * mm, "end": v(33.05, 20) * mm});
            skLineSegment(sketch, "E4.18.1.0", {"start": v(33.05, 14.9) * mm, "end": v(35.55, 9.9) * mm});
            skLineSegment(sketch, "E4.18.1.1", {"start": v(30.55, 9.9) * mm, "end": v(35.55, 9.9) * mm});
            skLineSegment(sketch, "E4.18.1.2", {"start": v(30.55, 9.9) * mm, "end": v(33.05, 14.9) * mm});
            skLineSegment(sketch, "E4.18.2.0", {"start": v(33.05, 9.8) * mm, "end": v(35.55, 4.8) * mm});
            skLineSegment(sketch, "E4.18.2.1", {"start": v(30.55, 4.8) * mm, "end": v(35.55, 4.8) * mm});
            skLineSegment(sketch, "E4.18.2.2", {"start": v(30.55, 4.8) * mm, "end": v(33.05, 9.8) * mm});
            skLineSegment(sketch, "E4.18.3.0", {"start": v(33.05, 4.7) * mm, "end": v(35.55, -0.3) * mm});
            skLineSegment(sketch, "E4.18.3.1", {"start": v(30.55, -0.3) * mm, "end": v(35.55, -0.3) * mm});
            skLineSegment(sketch, "E4.18.3.2", {"start": v(30.55, -0.3) * mm, "end": v(33.05, 4.7) * mm});
            skLineSegment(sketch, "E4.18.4.0", {"start": v(33.05, -0.4) * mm, "end": v(35.55, -5.4) * mm});
            skLineSegment(sketch, "E4.18.4.1", {"start": v(30.55, -5.4) * mm, "end": v(35.55, -5.4) * mm});
            skLineSegment(sketch, "E4.18.4.2", {"start": v(30.55, -5.4) * mm, "end": v(33.05, -0.4) * mm});
            skLineSegment(sketch, "E4.18.5.0", {"start": v(33.05, -5.5) * mm, "end": v(35.55, -10.5) * mm});
            skLineSegment(sketch, "E4.18.5.1", {"start": v(30.55, -10.5) * mm, "end": v(35.55, -10.5) * mm});
            skLineSegment(sketch, "E4.18.5.2", {"start": v(30.55, -10.5) * mm, "end": v(33.05, -5.5) * mm});
            skLineSegment(sketch, "E4.18.6.0", {"start": v(33.05, -10.6) * mm, "end": v(35.55, -15.6) * mm});
            skLineSegment(sketch, "E4.18.6.1", {"start": v(30.55, -15.6) * mm, "end": v(35.55, -15.6) * mm});
            skLineSegment(sketch, "E4.18.6.2", {"start": v(30.55, -15.6) * mm, "end": v(33.05, -10.6) * mm});
            skLineSegment(sketch, "E4.18.7.0", {"start": v(33.05, -15.7) * mm, "end": v(35.55, -20.7) * mm});
            skLineSegment(sketch, "E4.18.7.1", {"start": v(30.55, -20.7) * mm, "end": v(35.55, -20.7) * mm});
            skLineSegment(sketch, "E4.18.7.2", {"start": v(30.55, -20.7) * mm, "end": v(33.05, -15.7) * mm});
            skLineSegment(sketch, "E4.19.0.0", {"start": v(38.15, 20) * mm, "end": v(40.65, 15) * mm});
            skLineSegment(sketch, "E4.19.0.1", {"start": v(35.65, 15) * mm, "end": v(40.65, 15) * mm});
            skLineSegment(sketch, "E4.19.0.2", {"start": v(35.65, 15) * mm, "end": v(38.15, 20) * mm});
            skLineSegment(sketch, "E4.19.1.0", {"start": v(38.15, 14.9) * mm, "end": v(40.65, 9.9) * mm});
            skLineSegment(sketch, "E4.19.1.1", {"start": v(35.65, 9.9) * mm, "end": v(40.65, 9.9) * mm});
            skLineSegment(sketch, "E4.19.1.2", {"start": v(35.65, 9.9) * mm, "end": v(38.15, 14.9) * mm});
            skLineSegment(sketch, "E4.19.2.0", {"start": v(38.15, 9.8) * mm, "end": v(40.65, 4.8) * mm});
            skLineSegment(sketch, "E4.19.2.1", {"start": v(35.65, 4.8) * mm, "end": v(40.65, 4.8) * mm});
            skLineSegment(sketch, "E4.19.2.2", {"start": v(35.65, 4.8) * mm, "end": v(38.15, 9.8) * mm});
            skLineSegment(sketch, "E4.19.3.0", {"start": v(38.15, 4.7) * mm, "end": v(40.65, -0.3) * mm});
            skLineSegment(sketch, "E4.19.3.1", {"start": v(35.65, -0.3) * mm, "end": v(40.65, -0.3) * mm});
            skLineSegment(sketch, "E4.19.3.2", {"start": v(35.65, -0.3) * mm, "end": v(38.15, 4.7) * mm});
            skLineSegment(sketch, "E4.19.4.0", {"start": v(38.15, -0.4) * mm, "end": v(40.65, -5.4) * mm});
            skLineSegment(sketch, "E4.19.4.1", {"start": v(35.65, -5.4) * mm, "end": v(40.65, -5.4) * mm});
            skLineSegment(sketch, "E4.19.4.2", {"start": v(35.65, -5.4) * mm, "end": v(38.15, -0.4) * mm});
            skLineSegment(sketch, "E4.19.5.0", {"start": v(38.15, -5.5) * mm, "end": v(40.65, -10.5) * mm});
            skLineSegment(sketch, "E4.19.5.1", {"start": v(35.65, -10.5) * mm, "end": v(40.65, -10.5) * mm});
            skLineSegment(sketch, "E4.19.5.2", {"start": v(35.65, -10.5) * mm, "end": v(38.15, -5.5) * mm});
            skLineSegment(sketch, "E4.19.6.0", {"start": v(38.15, -10.6) * mm, "end": v(40.65, -15.6) * mm});
            skLineSegment(sketch, "E4.19.6.1", {"start": v(35.65, -15.6) * mm, "end": v(40.65, -15.6) * mm});
            skLineSegment(sketch, "E4.19.6.2", {"start": v(35.65, -15.6) * mm, "end": v(38.15, -10.6) * mm});
            skLineSegment(sketch, "E4.19.7.0", {"start": v(38.15, -15.7) * mm, "end": v(40.65, -20.7) * mm});
            skLineSegment(sketch, "E4.19.7.1", {"start": v(35.65, -20.7) * mm, "end": v(40.65, -20.7) * mm});
            skLineSegment(sketch, "E4.19.7.2", {"start": v(35.65, -20.7) * mm, "end": v(38.15, -15.7) * mm});
            skLineSegment(sketch, "E4.20.0.0", {"start": v(43.25, 20) * mm, "end": v(45.75, 15) * mm});
            skLineSegment(sketch, "E4.20.0.1", {"start": v(40.75, 15) * mm, "end": v(45.75, 15) * mm});
            skLineSegment(sketch, "E4.20.0.2", {"start": v(40.75, 15) * mm, "end": v(43.25, 20) * mm});
            skLineSegment(sketch, "E4.20.1.0", {"start": v(43.25, 14.9) * mm, "end": v(45.75, 9.9) * mm});
            skLineSegment(sketch, "E4.20.1.1", {"start": v(40.75, 9.9) * mm, "end": v(45.75, 9.9) * mm});
            skLineSegment(sketch, "E4.20.1.2", {"start": v(40.75, 9.9) * mm, "end": v(43.25, 14.9) * mm});
            skLineSegment(sketch, "E4.20.2.0", {"start": v(43.25, 9.8) * mm, "end": v(45.75, 4.8) * mm});
            skLineSegment(sketch, "E4.20.2.1", {"start": v(40.75, 4.8) * mm, "end": v(45.75, 4.8) * mm});
            skLineSegment(sketch, "E4.20.2.2", {"start": v(40.75, 4.8) * mm, "end": v(43.25, 9.8) * mm});
            skLineSegment(sketch, "E4.20.3.0", {"start": v(43.25, 4.7) * mm, "end": v(45.75, -0.3) * mm});
            skLineSegment(sketch, "E4.20.3.1", {"start": v(40.75, -0.3) * mm, "end": v(45.75, -0.3) * mm});
            skLineSegment(sketch, "E4.20.3.2", {"start": v(40.75, -0.3) * mm, "end": v(43.25, 4.7) * mm});
            skLineSegment(sketch, "E4.20.4.0", {"start": v(43.25, -0.4) * mm, "end": v(45.75, -5.4) * mm});
            skLineSegment(sketch, "E4.20.4.1", {"start": v(40.75, -5.4) * mm, "end": v(45.75, -5.4) * mm});
            skLineSegment(sketch, "E4.20.4.2", {"start": v(40.75, -5.4) * mm, "end": v(43.25, -0.4) * mm});
            skLineSegment(sketch, "E4.20.5.0", {"start": v(43.25, -5.5) * mm, "end": v(45.75, -10.5) * mm});
            skLineSegment(sketch, "E4.20.5.1", {"start": v(40.75, -10.5) * mm, "end": v(45.75, -10.5) * mm});
            skLineSegment(sketch, "E4.20.5.2", {"start": v(40.75, -10.5) * mm, "end": v(43.25, -5.5) * mm});
            skLineSegment(sketch, "E4.20.6.0", {"start": v(43.25, -10.6) * mm, "end": v(45.75, -15.6) * mm});
            skLineSegment(sketch, "E4.20.6.1", {"start": v(40.75, -15.6) * mm, "end": v(45.75, -15.6) * mm});
            skLineSegment(sketch, "E4.20.6.2", {"start": v(40.75, -15.6) * mm, "end": v(43.25, -10.6) * mm});
            skLineSegment(sketch, "E4.20.7.0", {"start": v(43.25, -15.7) * mm, "end": v(45.75, -20.7) * mm});
            skLineSegment(sketch, "E4.20.7.1", {"start": v(40.75, -20.7) * mm, "end": v(45.75, -20.7) * mm});
            skLineSegment(sketch, "E4.20.7.2", {"start": v(40.75, -20.7) * mm, "end": v(43.25, -15.7) * mm});
            skLineSegment(sketch, "E4.21.0.0", {"start": v(48.35, 20) * mm, "end": v(50.85, 15) * mm});
            skLineSegment(sketch, "E4.21.0.1", {"start": v(45.85, 15) * mm, "end": v(50.85, 15) * mm});
            skLineSegment(sketch, "E4.21.0.2", {"start": v(45.85, 15) * mm, "end": v(48.35, 20) * mm});
            skLineSegment(sketch, "E4.21.1.0", {"start": v(48.35, 14.9) * mm, "end": v(50.85, 9.9) * mm});
            skLineSegment(sketch, "E4.21.1.1", {"start": v(45.85, 9.9) * mm, "end": v(50.85, 9.9) * mm});
            skLineSegment(sketch, "E4.21.1.2", {"start": v(45.85, 9.9) * mm, "end": v(48.35, 14.9) * mm});
            skLineSegment(sketch, "E4.21.2.0", {"start": v(48.35, 9.8) * mm, "end": v(50.85, 4.8) * mm});
            skLineSegment(sketch, "E4.21.2.1", {"start": v(45.85, 4.8) * mm, "end": v(50.85, 4.8) * mm});
            skLineSegment(sketch, "E4.21.2.2", {"start": v(45.85, 4.8) * mm, "end": v(48.35, 9.8) * mm});
            skLineSegment(sketch, "E4.21.3.0", {"start": v(48.35, 4.7) * mm, "end": v(50.85, -0.3) * mm});
            skLineSegment(sketch, "E4.21.3.1", {"start": v(45.85, -0.3) * mm, "end": v(50.85, -0.3) * mm});
            skLineSegment(sketch, "E4.21.3.2", {"start": v(45.85, -0.3) * mm, "end": v(48.35, 4.7) * mm});
            skLineSegment(sketch, "E4.21.4.0", {"start": v(48.35, -0.4) * mm, "end": v(50.85, -5.4) * mm});
            skLineSegment(sketch, "E4.21.4.1", {"start": v(45.85, -5.4) * mm, "end": v(50.85, -5.4) * mm});
            skLineSegment(sketch, "E4.21.4.2", {"start": v(45.85, -5.4) * mm, "end": v(48.35, -0.4) * mm});
            skLineSegment(sketch, "E4.21.5.0", {"start": v(48.35, -5.5) * mm, "end": v(50.85, -10.5) * mm});
            skLineSegment(sketch, "E4.21.5.1", {"start": v(45.85, -10.5) * mm, "end": v(50.85, -10.5) * mm});
            skLineSegment(sketch, "E4.21.5.2", {"start": v(45.85, -10.5) * mm, "end": v(48.35, -5.5) * mm});
            skLineSegment(sketch, "E4.21.6.0", {"start": v(48.35, -10.6) * mm, "end": v(50.85, -15.6) * mm});
            skLineSegment(sketch, "E4.21.6.1", {"start": v(45.85, -15.6) * mm, "end": v(50.85, -15.6) * mm});
            skLineSegment(sketch, "E4.21.6.2", {"start": v(45.85, -15.6) * mm, "end": v(48.35, -10.6) * mm});
            skLineSegment(sketch, "E4.21.7.0", {"start": v(48.35, -15.7) * mm, "end": v(50.85, -20.7) * mm});
            skLineSegment(sketch, "E4.21.7.1", {"start": v(45.85, -20.7) * mm, "end": v(50.85, -20.7) * mm});
            skLineSegment(sketch, "E4.21.7.2", {"start": v(45.85, -20.7) * mm, "end": v(48.35, -15.7) * mm});
            skLineSegment(sketch, "E4.22.0.0", {"start": v(53.45, 20) * mm, "end": v(55.95, 15) * mm});
            skLineSegment(sketch, "E4.22.0.1", {"start": v(50.95, 15) * mm, "end": v(55.95, 15) * mm});
            skLineSegment(sketch, "E4.22.0.2", {"start": v(50.95, 15) * mm, "end": v(53.45, 20) * mm});
            skLineSegment(sketch, "E4.22.1.0", {"start": v(53.45, 14.9) * mm, "end": v(55.95, 9.9) * mm});
            skLineSegment(sketch, "E4.22.1.1", {"start": v(50.95, 9.9) * mm, "end": v(55.95, 9.9) * mm});
            skLineSegment(sketch, "E4.22.1.2", {"start": v(50.95, 9.9) * mm, "end": v(53.45, 14.9) * mm});
            skLineSegment(sketch, "E4.22.2.0", {"start": v(53.45, 9.8) * mm, "end": v(55.95, 4.8) * mm});
            skLineSegment(sketch, "E4.22.2.1", {"start": v(50.95, 4.8) * mm, "end": v(55.95, 4.8) * mm});
            skLineSegment(sketch, "E4.22.2.2", {"start": v(50.95, 4.8) * mm, "end": v(53.45, 9.8) * mm});
            skLineSegment(sketch, "E4.22.3.0", {"start": v(53.45, 4.7) * mm, "end": v(55.95, -0.3) * mm});
            skLineSegment(sketch, "E4.22.3.1", {"start": v(50.95, -0.3) * mm, "end": v(55.95, -0.3) * mm});
            skLineSegment(sketch, "E4.22.3.2", {"start": v(50.95, -0.3) * mm, "end": v(53.45, 4.7) * mm});
            skLineSegment(sketch, "E4.22.4.0", {"start": v(53.45, -0.4) * mm, "end": v(55.95, -5.4) * mm});
            skLineSegment(sketch, "E4.22.4.1", {"start": v(50.95, -5.4) * mm, "end": v(55.95, -5.4) * mm});
            skLineSegment(sketch, "E4.22.4.2", {"start": v(50.95, -5.4) * mm, "end": v(53.45, -0.4) * mm});
            skLineSegment(sketch, "E4.22.5.0", {"start": v(53.45, -5.5) * mm, "end": v(55.95, -10.5) * mm});
            skLineSegment(sketch, "E4.22.5.1", {"start": v(50.95, -10.5) * mm, "end": v(55.95, -10.5) * mm});
            skLineSegment(sketch, "E4.22.5.2", {"start": v(50.95, -10.5) * mm, "end": v(53.45, -5.5) * mm});
            skLineSegment(sketch, "E4.22.6.0", {"start": v(53.45, -10.6) * mm, "end": v(55.95, -15.6) * mm});
            skLineSegment(sketch, "E4.22.6.1", {"start": v(50.95, -15.6) * mm, "end": v(55.95, -15.6) * mm});
            skLineSegment(sketch, "E4.22.6.2", {"start": v(50.95, -15.6) * mm, "end": v(53.45, -10.6) * mm});
            skLineSegment(sketch, "E4.22.7.0", {"start": v(53.45, -15.7) * mm, "end": v(55.95, -20.7) * mm});
            skLineSegment(sketch, "E4.22.7.1", {"start": v(50.95, -20.7) * mm, "end": v(55.95, -20.7) * mm});
            skLineSegment(sketch, "E4.22.7.2", {"start": v(50.95, -20.7) * mm, "end": v(53.45, -15.7) * mm});
            skLineSegment(sketch, "E4.23.0.0", {"start": v(58.55, 20) * mm, "end": v(61.05, 15) * mm});
            skLineSegment(sketch, "E4.23.0.1", {"start": v(56.05, 15) * mm, "end": v(61.05, 15) * mm});
            skLineSegment(sketch, "E4.23.0.2", {"start": v(56.05, 15) * mm, "end": v(58.55, 20) * mm});
            skLineSegment(sketch, "E4.23.1.0", {"start": v(58.55, 14.9) * mm, "end": v(61.05, 9.9) * mm});
            skLineSegment(sketch, "E4.23.1.1", {"start": v(56.05, 9.9) * mm, "end": v(61.05, 9.9) * mm});
            skLineSegment(sketch, "E4.23.1.2", {"start": v(56.05, 9.9) * mm, "end": v(58.55, 14.9) * mm});
            skLineSegment(sketch, "E4.23.2.0", {"start": v(58.55, 9.8) * mm, "end": v(61.05, 4.8) * mm});
            skLineSegment(sketch, "E4.23.2.1", {"start": v(56.05, 4.8) * mm, "end": v(61.05, 4.8) * mm});
            skLineSegment(sketch, "E4.23.2.2", {"start": v(56.05, 4.8) * mm, "end": v(58.55, 9.8) * mm});
            skLineSegment(sketch, "E4.23.3.0", {"start": v(58.55, 4.7) * mm, "end": v(61.05, -0.3) * mm});
            skLineSegment(sketch, "E4.23.3.1", {"start": v(56.05, -0.3) * mm, "end": v(61.05, -0.3) * mm});
            skLineSegment(sketch, "E4.23.3.2", {"start": v(56.05, -0.3) * mm, "end": v(58.55, 4.7) * mm});
            skLineSegment(sketch, "E4.23.4.0", {"start": v(58.55, -0.4) * mm, "end": v(61.05, -5.4) * mm});
            skLineSegment(sketch, "E4.23.4.1", {"start": v(56.05, -5.4) * mm, "end": v(61.05, -5.4) * mm});
            skLineSegment(sketch, "E4.23.4.2", {"start": v(56.05, -5.4) * mm, "end": v(58.55, -0.4) * mm});
            skLineSegment(sketch, "E4.23.5.0", {"start": v(58.55, -5.5) * mm, "end": v(61.05, -10.5) * mm});
            skLineSegment(sketch, "E4.23.5.1", {"start": v(56.05, -10.5) * mm, "end": v(61.05, -10.5) * mm});
            skLineSegment(sketch, "E4.23.5.2", {"start": v(56.05, -10.5) * mm, "end": v(58.55, -5.5) * mm});
            skLineSegment(sketch, "E4.23.6.0", {"start": v(58.55, -10.6) * mm, "end": v(61.05, -15.6) * mm});
            skLineSegment(sketch, "E4.23.6.1", {"start": v(56.05, -15.6) * mm, "end": v(61.05, -15.6) * mm});
            skLineSegment(sketch, "E4.23.6.2", {"start": v(56.05, -15.6) * mm, "end": v(58.55, -10.6) * mm});
            skLineSegment(sketch, "E4.23.7.0", {"start": v(58.55, -15.7) * mm, "end": v(61.05, -20.7) * mm});
            skLineSegment(sketch, "E4.23.7.1", {"start": v(56.05, -20.7) * mm, "end": v(61.05, -20.7) * mm});
            skLineSegment(sketch, "E4.23.7.2", {"start": v(56.05, -20.7) * mm, "end": v(58.55, -15.7) * mm});
            skLineSegment(sketch, "E4.direction1", {"start": v(-56.25, 15) * mm, "end": v(-51.15, 15) * mm, "construction": true});
            skLineSegment(sketch, "E4.direction2", {"start": v(-56.25, 15) * mm, "end": v(-56.25, 9.9) * mm, "construction": true});
            skSolve(sketch);
        }
        {
            var Q0;
            Q0 = qSketchRegion(id + "F2", true);
            extrude(context, id + "F3", {"entities" : qUnion([Q0]), "operationType" : NewBodyOperationType.ADD, "depth" : 3 * mm});
        }
    });
